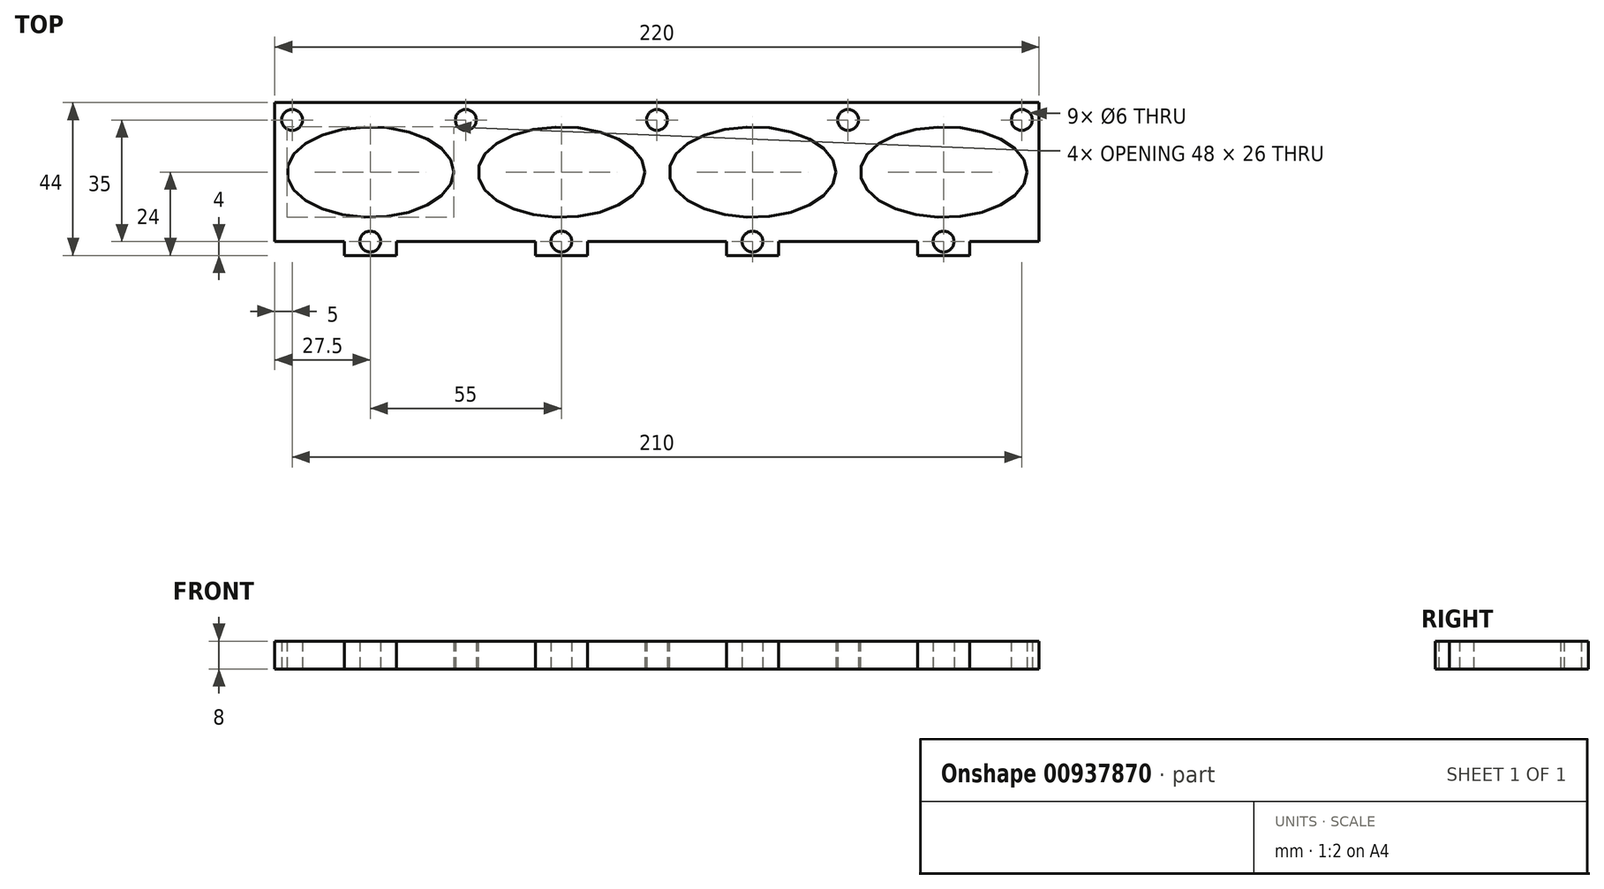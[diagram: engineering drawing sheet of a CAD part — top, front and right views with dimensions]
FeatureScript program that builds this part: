
annotation { "Feature Type Name" : "Feature", "Feature Type Description" : "" }
export const myFeature = defineFeature(function(context is Context, id is Id, definition is map)
    precondition{}
    {
        {
            var Q0;
            Q0=qCreatedBy(makeId("Top.planeOp"),FACE);
            var sketch = newSketch(context, id + "F0", { "sketchPlane" : qUnion([Q0])});
            skLineSegment(sketch, "E0.bottom", {"start": v(110, -20) * mm, "end": v(-110, -20) * mm});
            skLineSegment(sketch, "E0.top", {"start": v(110, 20) * mm, "end": v(-110, 20) * mm});
            skLineSegment(sketch, "E0.left", {"start": v(110, -20) * mm, "end": v(110, 20) * mm});
            skLineSegment(sketch, "E0.right", {"start": v(-110, -20) * mm, "end": v(-110, 20) * mm});
            skPoint(sketch, "E0.middle", {"position": v(0, 0) * mm});
            skLineSegment(sketch, "E1", {"start": v(-55, 20) * mm, "end": v(-55, -20) * mm, "construction": true});
            skLineSegment(sketch, "E2", {"start": v(55, 20) * mm, "end": v(55, -20) * mm, "construction": true});
            skLineSegment(sketch, "E3", {"start": v(0, 20) * mm, "end": v(0, -20) * mm, "construction": true});
            skPoint(sketch, "E4", {"position": v(-27.5, 0) * mm});
            skPoint(sketch, "E5", {"position": v(27.5, 0) * mm});
            skPoint(sketch, "E6", {"position": v(82.5, 0) * mm});
            skPoint(sketch, "E7", {"position": v(-82.5, 0) * mm});
            skEllipse(sketch, "E8", {"center": v(-82.5, 0) * mm, "majorRadius": 24 * mm, "minorRadius": 13 * mm, "majorAxis": v(1, 0)});
            skEllipse(sketch, "E9", {"center": v(-27.5, 0) * mm, "majorRadius": 24 * mm, "minorRadius": 13 * mm, "majorAxis": v(1, 0)});
            skEllipse(sketch, "E10", {"center": v(27.5, 0) * mm, "majorRadius": 24 * mm, "minorRadius": 13 * mm, "majorAxis": v(1, 0)});
            skEllipse(sketch, "E11", {"center": v(82.5, 0) * mm, "majorRadius": 24 * mm, "minorRadius": 13 * mm, "majorAxis": v(1, 0)});
            skPoint(sketch, "E12", {"position": v(-105, 15) * mm});
            skPoint(sketch, "E13", {"position": v(-82.5, -20) * mm});
            skPoint(sketch, "E13.positionSnap0", {"position": v(-82.5, 13) * mm});
            skPoint(sketch, "E14", {"position": v(-55, 15) * mm});
            skPoint(sketch, "E15", {"position": v(0, 15) * mm});
            skPoint(sketch, "E16", {"position": v(55, 15) * mm});
            skPoint(sketch, "E17", {"position": v(105, 15) * mm});
            skPoint(sketch, "E18", {"position": v(-27.5, -20) * mm});
            skPoint(sketch, "E19", {"position": v(27.5, -20) * mm});
            skPoint(sketch, "E20", {"position": v(82.5, -20) * mm});
            skCircle(sketch, "E21", {"center": v(-105, 15) * mm, "radius": 3 * mm});
            skCircle(sketch, "E22", {"center": v(-55, 15) * mm, "radius": 3 * mm});
            skCircle(sketch, "E23", {"center": v(0, 15) * mm, "radius": 3 * mm});
            skCircle(sketch, "E24", {"center": v(55, 15) * mm, "radius": 3 * mm});
            skCircle(sketch, "E25", {"center": v(105, 15) * mm, "radius": 3 * mm});
            skCircle(sketch, "E26", {"center": v(82.5, -20) * mm, "radius": 3 * mm});
            skCircle(sketch, "E27", {"center": v(27.5, -20) * mm, "radius": 3 * mm});
            skCircle(sketch, "E28", {"center": v(-27.5, -20) * mm, "radius": 3 * mm});
            skCircle(sketch, "E29", {"center": v(-82.5, -20) * mm, "radius": 3 * mm});
            skLineSegment(sketch, "E30.bottom", {"start": v(-90, -20) * mm, "end": v(-75, -20) * mm});
            skLineSegment(sketch, "E30.top", {"start": v(-90, -24) * mm, "end": v(-75, -24) * mm});
            skLineSegment(sketch, "E30.left", {"start": v(-90, -20) * mm, "end": v(-90, -24) * mm});
            skLineSegment(sketch, "E30.right", {"start": v(-75, -20) * mm, "end": v(-75, -24) * mm});
            skLineSegment(sketch, "E31.bottom", {"start": v(-20, -24) * mm, "end": v(-35, -24) * mm});
            skLineSegment(sketch, "E31.top", {"start": v(-20, -16) * mm, "end": v(-35, -16) * mm});
            skLineSegment(sketch, "E31.left", {"start": v(-20, -24) * mm, "end": v(-20, -16) * mm});
            skLineSegment(sketch, "E31.right", {"start": v(-35, -24) * mm, "end": v(-35, -16) * mm});
            skLineSegment(sketch, "E32.bottom", {"start": v(35, -24) * mm, "end": v(20, -24) * mm});
            skLineSegment(sketch, "E32.top", {"start": v(35, -16) * mm, "end": v(20, -16) * mm});
            skLineSegment(sketch, "E32.left", {"start": v(35, -24) * mm, "end": v(35, -16) * mm});
            skLineSegment(sketch, "E32.right", {"start": v(20, -24) * mm, "end": v(20, -16) * mm});
            skLineSegment(sketch, "E33.bottom", {"start": v(90, -24) * mm, "end": v(75, -24) * mm});
            skLineSegment(sketch, "E33.top", {"start": v(90, -16) * mm, "end": v(75, -16) * mm});
            skLineSegment(sketch, "E33.left", {"start": v(90, -24) * mm, "end": v(90, -16) * mm});
            skLineSegment(sketch, "E33.right", {"start": v(75, -24) * mm, "end": v(75, -16) * mm});
            skSolve(sketch);
        }
        {
            var Q0;
            Q0=makeQuery(id+"F0.imprint","IMPRINT",FACE,{"disambiguationData":[TD([[makeQuery(id+"F0.imprint","IMPRINT",EDGE,{"derivedFrom":sQuery(id+"F0.wireOp",EDGE,"E0.top")}),1.0]])]});
            var Q1;
            {var subQ0=sQuery(id+"F0.wireOp",EDGE,"E31.bottom");Q1=makeQuery(id+"F0.imprint","IMPRINT",FACE,{"disambiguationData":[TD([[makeQuery(id+"F0.imprint","IMPRINT",EDGE,{"derivedFrom":subQ0}),-1.0]])]});}
            var Q2;
            Q2=makeQuery(id+"F0.imprint","IMPRINT",FACE,{"disambiguationData":[TD([[makeQuery(id+"F0.imprint","IMPRINT",EDGE,{"derivedFrom":sQuery(id+"F0.wireOp",EDGE,"E30.top")}),1.0]])]});
            var Q3;
            {var subQ0=sQuery(id+"F0.wireOp",EDGE,"E32.bottom");Q3=makeQuery(id+"F0.imprint","IMPRINT",FACE,{"disambiguationData":[TD([[makeQuery(id+"F0.imprint","IMPRINT",EDGE,{"derivedFrom":subQ0}),-1.0]])]});}
            var Q4;
            {var subQ0=sQuery(id+"F0.wireOp",EDGE,"E33.bottom");Q4=makeQuery(id+"F0.imprint","IMPRINT",FACE,{"disambiguationData":[TD([[makeQuery(id+"F0.imprint","IMPRINT",EDGE,{"derivedFrom":subQ0}),-1.0]])]});}
            var Q5;
            {var subQ4=sQuery(id+"F0.wireOp",EDGE,"E32.top");Q5=makeQuery(id+"F0.imprint","IMPRINT",FACE,{"disambiguationData":[TD([[makeQuery(id+"F0.imprint","IMPRINT",EDGE,{"derivedFrom":subQ4}),1.0]])]});}
            var Q6;
            {var subQ4=sQuery(id+"F0.wireOp",EDGE,"E31.top");Q6=makeQuery(id+"F0.imprint","IMPRINT",FACE,{"disambiguationData":[TD([[makeQuery(id+"F0.imprint","IMPRINT",EDGE,{"derivedFrom":subQ4}),1.0]])]});}
            var Q7;
            {var subQ0=sQuery(id+"F0.wireOp",EDGE,"E33.top");Q7=makeQuery(id+"F0.imprint","IMPRINT",FACE,{"disambiguationData":[TD([[makeQuery(id+"F0.imprint","IMPRINT",EDGE,{"derivedFrom":subQ0}),1.0]])]});}
            extrude(context, id + "F1", {"entities" : qUnion([Q0, Q1, Q2, Q3, Q4, Q5, Q6, Q7]), "depth" : 8 * mm, "offsetDistance" : 25 * mm});
        }
    });
